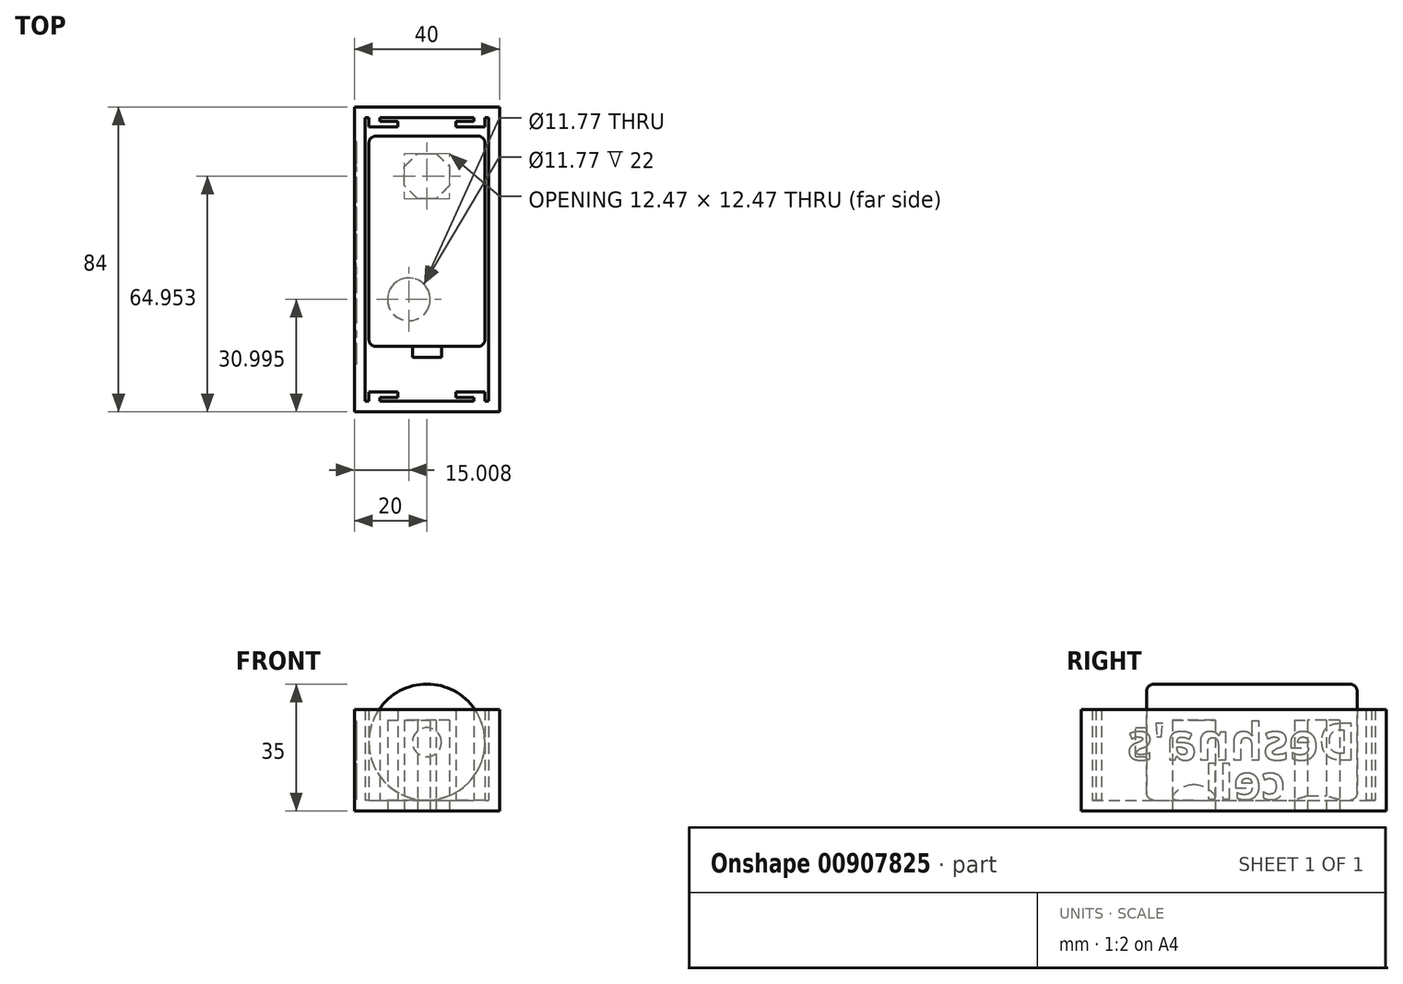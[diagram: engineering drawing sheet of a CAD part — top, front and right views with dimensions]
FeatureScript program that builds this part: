
annotation { "Feature Type Name" : "Feature", "Feature Type Description" : "" }
export const myFeature = defineFeature(function(context is Context, id is Id, definition is map)
    precondition{}
    {
        {
            var Q0;
            Q0=qCreatedBy(makeId("Front.planeOp"),FACE);
            var sketch = newSketch(context, id + "F0", { "sketchPlane" : qUnion([Q0])});
            skCircle(sketch, "E0", {"center": v(0, 0) * mm, "radius": 16 * mm});
            skSolve(sketch);
        }
        {
            var Q0;
            Q0=makeQuery(id+"F0.imprint","IMPRINT",FACE,{"disambiguationData":[TD([[makeQuery(id+"F0.imprint","IMPRINT",EDGE,{"derivedFrom":sQuery(id+"F0.wireOp",EDGE,"E0")}),1.0]])]});
            extrude(context, id + "F1", {"entities" : qUnion([Q0]), "depth" : 58 * mm, "offsetDistance" : 25 * mm});
        }
        {
            var Q0;
            Q0=makeQuery(id+"F1.opExtrude","CAP_FACE",FACE,{"disambiguationData":[OSD([sQuery(id+"F0.wireOp",EDGE,"E0")])],"isStart":false});
            var sketch = newSketch(context, id + "F2", { "sketchPlane" : qUnion([Q0])});
            skCircle(sketch, "E1", {"center": v(0, 0) * mm, "radius": 4 * mm});
            skSolve(sketch);
        }
        {
            var Q0;
            Q0=makeQuery(id+"F2.imprint","IMPRINT",FACE,{"disambiguationData":[TD([[makeQuery(id+"F2.imprint","IMPRINT",EDGE,{"derivedFrom":sQuery(id+"F2.wireOp",EDGE,"E1")}),1.0]])]});
            extrude(context, id + "F3", {"entities" : qUnion([Q0]), "operationType" : NewBodyOperationType.ADD, "depth" : 3 * mm, "offsetDistance" : 25 * mm});
        }
        {
            var Q0;
            Q0=makeQuery(id+"F1.opExtrude","CAP_EDGE",EDGE,{"disambiguationData":[OSD([sQuery(id+"F0.wireOp",EDGE,"E0")])],"isStart":false});
            var Q1;
            Q1=makeQuery(id+"F1.opExtrude","CAP_EDGE",EDGE,{"disambiguationData":[OSD([sQuery(id+"F0.wireOp",EDGE,"E0")])],"isStart":true});
            fillet(context, id + "F4", {"entities" : qUnion([Q0, Q1]), "radius" : 2 * mm, "tangentPropagation" : true, "allowEdgeOverflow" : false});
        }
        {
            var Q0;
            Q0=qCreatedBy(makeId("Top.planeOp"),FACE);
            cPlane(context, id + "F5", {"entities" : qUnion([Q0]), "cplaneType" : CPlaneType.OFFSET, "offset" : 16 * mm, "oppositeDirection" : true, "width" : 150 * mm, "height" : 150 * mm});
        }
        {
            var Q0;
            Q0=qCreatedBy(id+"F5.planeOp",FACE);
            var sketch = newSketch(context, id + "F6", { "sketchPlane" : qUnion([Q0])});
            skLineSegment(sketch, "E2.bottom", {"start": v(-20, 8) * mm, "end": v(20, 8) * mm});
            skLineSegment(sketch, "E2.top", {"start": v(-20, -76) * mm, "end": v(20, -76) * mm});
            skLineSegment(sketch, "E2.left", {"start": v(-20, 8) * mm, "end": v(-20, -76) * mm});
            skLineSegment(sketch, "E2.right", {"start": v(20, 8) * mm, "end": v(20, -76) * mm});
            skSolve(sketch);
        }
        {
            var Q0;
            Q0 = qSketchRegion(id + "F6", true);
            extrude(context, id + "F7", {"entities" : qUnion([Q0]), "oppositeDirection" : true, "depth" : 3 * mm, "offsetDistance" : 25 * mm});
        }
        {
            var Q0;
            Q0=makeQuery(id+"F7.opExtrude","CAP_FACE",FACE,{"disambiguationData":[OSD([sQuery(id+"F6.wireOp",EDGE,"E2.bottom"),sQuery(id+"F6.wireOp",EDGE,"E2.top"),sQuery(id+"F6.wireOp",EDGE,"E2.left"),sQuery(id+"F6.wireOp",EDGE,"E2.right")])],"isStart":true});
            var sketch = newSketch(context, id + "F8", { "sketchPlane" : qUnion([Q0])});
            skLineSegment(sketch, "E3.0", {"start": v(-17, 5) * mm, "end": v(-17, -73) * mm});
            skLineSegment(sketch, "E3.1", {"start": v(17, 5) * mm, "end": v(-17, 5) * mm});
            skLineSegment(sketch, "E3.2", {"start": v(17, -73) * mm, "end": v(17, 5) * mm});
            skLineSegment(sketch, "E3.3", {"start": v(-17, -73) * mm, "end": v(17, -73) * mm});
            skLineSegment(sketch, "E4.0.0", {"start": v(-20, 8) * mm, "end": v(-20, -76) * mm});
            skLineSegment(sketch, "E4.0.1", {"start": v(-20, -76) * mm, "end": v(20, -76) * mm});
            skLineSegment(sketch, "E4.0.2", {"start": v(20, -76) * mm, "end": v(20, 8) * mm});
            skLineSegment(sketch, "E4.0.3", {"start": v(20, 8) * mm, "end": v(-20, 8) * mm});
            skSolve(sketch);
        }
        {
            var Q0;
            Q0 = qSketchRegion(id + "F8", true);
            extrude(context, id + "F9", {"entities" : qUnion([Q0]), "operationType" : NewBodyOperationType.ADD, "depth" : 25 * mm, "offsetDistance" : 25 * mm});
        }
        {
            var Q0;
            Q0=makeQuery(id+"F7.opExtrude","CAP_FACE",FACE,{"disambiguationData":[OSD([sQuery(id+"F6.wireOp",EDGE,"E2.bottom"),sQuery(id+"F6.wireOp",EDGE,"E2.top"),sQuery(id+"F6.wireOp",EDGE,"E2.left"),sQuery(id+"F6.wireOp",EDGE,"E2.right")])],"isStart":false});
            var sketch = newSketch(context, id + "F10", { "sketchPlane" : qUnion([Q0])});
            skCircle(sketch, "E5", {"center": v(-5, 45) * mm, "radius": 5.88 * mm});
            skCircle(sketch, "E6.cCircle", {"center": v(0, 11.05) * mm, "radius": 6.23 * mm, "construction": true});
            skLineSegment(sketch, "E6.0", {"start": v(-6.23, 8.47) * mm, "end": v(-6.23, 13.63) * mm});
            skLineSegment(sketch, "E6.1", {"start": v(-6.23, 13.63) * mm, "end": v(-2.58, 17.28) * mm});
            skLineSegment(sketch, "E6.2", {"start": v(-2.58, 17.28) * mm, "end": v(2.58, 17.28) * mm});
            skLineSegment(sketch, "E6.3", {"start": v(2.58, 17.28) * mm, "end": v(6.23, 13.63) * mm});
            skLineSegment(sketch, "E6.4", {"start": v(6.23, 13.63) * mm, "end": v(6.23, 8.47) * mm});
            skLineSegment(sketch, "E6.5", {"start": v(6.23, 8.47) * mm, "end": v(2.58, 4.81) * mm});
            skLineSegment(sketch, "E6.6", {"start": v(2.58, 4.81) * mm, "end": v(-2.58, 4.81) * mm});
            skLineSegment(sketch, "E6.7", {"start": v(-2.58, 4.81) * mm, "end": v(-6.23, 8.47) * mm});
            skPoint(sketch, "E6.0.midPoint", {"position": v(-6.23, 11.05) * mm});
            skSolve(sketch);
        }
        {
            var Q0;
            Q0 = qSketchRegion(id + "F10", true);
            extrude(context, id + "F11", {"entities" : qUnion([Q0]), "operationType" : NewBodyOperationType.REMOVE, "oppositeDirection" : true, "depth" : 25 * mm, "offsetDistance" : 25 * mm});
        }
        {
            var Q0;
            Q0=makeQuery(id+"F7.opExtrude","CAP_FACE",FACE,{"disambiguationData":[OSD([sQuery(id+"F6.wireOp",EDGE,"E2.bottom"),sQuery(id+"F6.wireOp",EDGE,"E2.top"),sQuery(id+"F6.wireOp",EDGE,"E2.left"),sQuery(id+"F6.wireOp",EDGE,"E2.right")])],"isStart":true});
            var sketch = newSketch(context, id + "F12", { "sketchPlane" : qUnion([Q0])});
            skLineSegment(sketch, "E7", {"start": v(16, 5) * mm, "end": v(16, 2.5) * mm});
            skLineSegment(sketch, "E8", {"start": v(16, 2.5) * mm, "end": v(8, 2.5) * mm});
            skLineSegment(sketch, "E9", {"start": v(8, 2.5) * mm, "end": v(8, 4) * mm});
            skLineSegment(sketch, "E10", {"start": v(8, 4) * mm, "end": v(13, 4) * mm});
            skLineSegment(sketch, "E11", {"start": v(13, 4) * mm, "end": v(13, 5) * mm});
            skLineSegment(sketch, "E12", {"start": v(13, 5) * mm, "end": v(16, 5) * mm});
            skLineSegment(sketch, "E13.MirrorCS", {"start": v(-8, 2.5) * mm, "end": v(-8, 4) * mm});
            skLineSegment(sketch, "E14.MirrorCS", {"start": v(-16, 2.5) * mm, "end": v(-8, 2.5) * mm});
            skLineSegment(sketch, "E15.MirrorCS", {"start": v(-16, 5) * mm, "end": v(-16, 2.5) * mm});
            skLineSegment(sketch, "E16.MirrorCS", {"start": v(-13, 5) * mm, "end": v(-16, 5) * mm});
            skLineSegment(sketch, "E17.MirrorCS", {"start": v(-13, 4) * mm, "end": v(-13, 5) * mm});
            skLineSegment(sketch, "E18.MirrorCS", {"start": v(-8, 4) * mm, "end": v(-13, 4) * mm});
            skLineSegment(sketch, "E19", {"start": v(17, -34) * mm, "end": v(-17, -34) * mm, "construction": true});
            skLineSegment(sketch, "E20.MirrorCS", {"start": v(-8, -70.5) * mm, "end": v(-8, -72) * mm});
            skLineSegment(sketch, "E21.MirrorCS", {"start": v(13, -73) * mm, "end": v(16, -73) * mm});
            skLineSegment(sketch, "E22.MirrorCS", {"start": v(-13, -73) * mm, "end": v(-16, -73) * mm});
            skLineSegment(sketch, "E23.MirrorCS", {"start": v(-13, -72) * mm, "end": v(-13, -73) * mm});
            skLineSegment(sketch, "E24.MirrorCS", {"start": v(8, -70.5) * mm, "end": v(8, -72) * mm});
            skLineSegment(sketch, "E25.MirrorCS", {"start": v(16, -73) * mm, "end": v(16, -70.5) * mm});
            skLineSegment(sketch, "E26.MirrorCS", {"start": v(13, -72) * mm, "end": v(13, -73) * mm});
            skLineSegment(sketch, "E27.MirrorCS", {"start": v(-16, -73) * mm, "end": v(-16, -70.5) * mm});
            skLineSegment(sketch, "E28.MirrorCS", {"start": v(-8, -72) * mm, "end": v(-13, -72) * mm});
            skLineSegment(sketch, "E29.MirrorCS", {"start": v(-16, -70.5) * mm, "end": v(-8, -70.5) * mm});
            skLineSegment(sketch, "E30.MirrorCS", {"start": v(8, -72) * mm, "end": v(13, -72) * mm});
            skLineSegment(sketch, "E31.MirrorCS", {"start": v(16, -70.5) * mm, "end": v(8, -70.5) * mm});
            skSolve(sketch);
        }
        {
            var Q0;
            Q0 = qSketchRegion(id + "F12", true);
            extrude(context, id + "F13", {"entities" : qUnion([Q0]), "operationType" : NewBodyOperationType.ADD, "depth" : 25 * mm, "offsetDistance" : 25 * mm});
        }
        {
            var Q0;
            Q0=makeQuery(id+"F9.boolean.opBoolean","MERGE",FACE,{"derivedFrom":[makeQuery(id+"F7.opExtrude","SWEPT_FACE",FACE,{"disambiguationData":[OSD([sQuery(id+"F6.wireOp",EDGE,"E2.left")])]}),makeQuery(id+"F9.opExtrude","SWEPT_FACE",FACE,{"disambiguationData":[OSD([sQuery(id+"F8.wireOp",EDGE,"E4.0.0")])]})]});
            var sketch = newSketch(context, id + "F14", { "sketchPlane" : qUnion([Q0])});
            skText(sketch, "E32", { "text": "Deshna\'s", "fontName": "OpenSans-Bold.ttf"});
            skText(sketch, "E33", { "text": "cell", "fontName": "OpenSans-Bold.ttf"});
            const initialGuessF14  = {"E32": [0.0003, -0.00486, 1, 0, 0.01007], "E33": [0.0198, -0.01571, 1, 0, 0.00931]};
            skSetInitialGuess(sketch, initialGuessF14);
            skSolve(sketch);
        }
        {
            var Q0;
            Q0 = qSketchRegion(id + "F14", true);
            extrude(context, id + "F15", {"entities" : qUnion([Q0]), "operationType" : NewBodyOperationType.REMOVE, "oppositeDirection" : true, "depth" : 0.5 * mm, "offsetDistance" : 25 * mm});
        }
    });
